annotation { "Feature Type Name" : "Feature", "Feature Type Description" : "" }
export const myFeature = defineFeature(function(context is Context, id is Id, definition is map)
    precondition{}
    {
        {
            var Q0;
            Q0=qCreatedBy(makeId("Top.planeOp"),FACE);
            var sketch = newSketch(context, id + "F0", { "sketchPlane" : qUnion([Q0])});
            skLineSegment(sketch, "E0.bottom", {"start": v(0, 0) * mm, "end": v(355.6, 0) * mm});
            skLineSegment(sketch, "E0.top", {"start": v(0, 50.8) * mm, "end": v(355.6, 50.8) * mm});
            skLineSegment(sketch, "E0.left", {"start": v(0, 0) * mm, "end": v(0, 50.8) * mm});
            skLineSegment(sketch, "E0.right", {"start": v(355.6, 0) * mm, "end": v(355.6, 50.8) * mm});
            skSolve(sketch);
        }
        {
            var Q0;
            Q0=makeQuery(id+"F0.imprint","IMPRINT",FACE,{"disambiguationData":[TD([[makeQuery(id+"F0.imprint","IMPRINT",EDGE,{"derivedFrom":sQuery(id+"F0.wireOp",EDGE,"E0.bottom")}),1.0]])]});
            extrude(context, id + "F1", {"entities" : qUnion([Q0]), "depth" : 6.35 * mm, "offsetDistance" : 25.4 * mm});
        }
        {
            var Q0;
            Q0=makeQuery(id+"F1.opExtrude","CAP_FACE",FACE,{"disambiguationData":[OSD([sQuery(id+"F0.wireOp",EDGE,"E0.bottom"),sQuery(id+"F0.wireOp",EDGE,"E0.top"),sQuery(id+"F0.wireOp",EDGE,"E0.left"),sQuery(id+"F0.wireOp",EDGE,"E0.right")])],"isStart":false});
            var sketch = newSketch(context, id + "F2", { "sketchPlane" : qUnion([Q0])});
            skText(sketch, "E1", { "text": "John Doe", "fontName": "OpenSans-BoldItalic.ttf"});
            const initialGuessF2  = {"E1": [0.06703, 0.01143, 1, 0, 0.02794]};
            skSetInitialGuess(sketch, initialGuessF2);
            skSolve(sketch);
        }
        {
            var Q0;
            Q0 = qSketchRegion(id + "F2", true);
            extrude(context, id + "F3", {"entities" : qUnion([Q0]), "operationType" : NewBodyOperationType.REMOVE, "oppositeDirection" : true, "depth" : 2.54 * mm, "offsetDistance" : 25.4 * mm});
        }
        {
            var Q0;
            {var subQ0=sQuery(id+"F0.wireOp",EDGE,"E0.top");var subQ1=sQuery(id+"F0.wireOp",EDGE,"E0.right");var subQ2=sQuery(id+"F0.wireOp",EDGE,"E0.bottom");var subQ3=sQuery(id+"F0.wireOp",EDGE,"E0.left");Q0=makeQuery(id+"F3.boolean.opBoolean","SPLIT",FACE,{"disambiguationData":[TD([makeQuery(id+"F1.opExtrude","SWEPT_FACE",FACE,{"disambiguationData":[OSD([subQ2])]})])],"derivedFrom":makeQuery(id+"F1.opExtrude","CAP_FACE",FACE,{"disambiguationData":[OSD([subQ2,subQ0,subQ3,subQ1])],"isStart":false})});}
            var sketch = newSketch(context, id + "F4", { "sketchPlane" : qUnion([Q0])});
            skCircle(sketch, "E2", {"center": v(311.15, 13.97) * mm, "radius": 5.08 * mm});
            skLineSegment(sketch, "E3", {"start": v(311.15, 13.97) * mm, "end": v(333.6, 36.42) * mm});
            skCircle(sketch, "E4.cCircle", {"center": v(335.4, 38.22) * mm, "radius": 2.54 * mm, "construction": true});
            skLineSegment(sketch, "E4.0", {"start": v(336.71, 33.3) * mm, "end": v(330.49, 39.53) * mm});
            skLineSegment(sketch, "E4.1", {"start": v(330.49, 39.53) * mm, "end": v(338.99, 41.8) * mm});
            skLineSegment(sketch, "E4.2", {"start": v(338.99, 41.8) * mm, "end": v(336.71, 33.3) * mm});
            skPoint(sketch, "E4.0.midPoint", {"position": v(333.6, 36.42) * mm});
            skCircle(sketch, "E5", {"center": v(311.15, 13.97) * mm, "radius": 7.62 * mm});
            skCircle(sketch, "E6", {"center": v(321.95, 38.1) * mm, "radius": 3.18 * mm});
            skCircle(sketch, "E7.cCircle", {"center": v(337.82, 26.03) * mm, "radius": 2.54 * mm, "construction": true});
            skLineSegment(sketch, "E7.0", {"start": v(341.41, 26.03) * mm, "end": v(337.82, 22.44) * mm});
            skLineSegment(sketch, "E7.1", {"start": v(337.82, 22.44) * mm, "end": v(334.23, 26.03) * mm});
            skLineSegment(sketch, "E7.2", {"start": v(334.23, 26.03) * mm, "end": v(337.82, 29.63) * mm});
            skLineSegment(sketch, "E7.3", {"start": v(337.82, 29.63) * mm, "end": v(341.41, 26.03) * mm});
            skPoint(sketch, "E7.0.midPoint", {"position": v(339.62, 24.24) * mm});
            skLineSegment(sketch, "E8", {"start": v(321.95, 38.1) * mm, "end": v(321.5, 38.55) * mm});
            skLineSegment(sketch, "E9", {"start": v(321.5, 38.55) * mm, "end": v(317.5, 34.55) * mm});
            skLineSegment(sketch, "E10", {"start": v(316.76, 32.53) * mm, "end": v(317.6, 22.96) * mm});
            skLineSegment(sketch, "E11", {"start": v(316.87, 20.95) * mm, "end": v(310.52, 14.6) * mm});
            skLineSegment(sketch, "E12", {"start": v(310.52, 14.6) * mm, "end": v(311.15, 13.97) * mm});
            skLineSegment(sketch, "E13", {"start": v(321.95, 38.1) * mm, "end": v(322.4, 37.65) * mm});
            skLineSegment(sketch, "E14", {"start": v(322.4, 37.65) * mm, "end": v(318.4, 33.65) * mm});
            skLineSegment(sketch, "E15", {"start": v(318.03, 32.65) * mm, "end": v(318.9, 22.79) * mm});
            skLineSegment(sketch, "E16", {"start": v(318.9, 22.79) * mm, "end": v(333.06, 36.96) * mm});
            skPoint(sketch, "E17.visualSharp", {"position": v(316.66, 33.71) * mm});
            skArc(sketch, "E17.filletArc", {"start": v(317.5, 34.55) * mm, "mid": v(316.9, 33.62) * mm, "end": v(316.76, 32.53) * mm});
            skPoint(sketch, "E18.visualSharp", {"position": v(317.98, 33.24) * mm});
            skArc(sketch, "E18.filletArc", {"start": v(318.4, 33.65) * mm, "mid": v(318.1, 33.2) * mm, "end": v(318.03, 32.65) * mm});
            skLineSegment(sketch, "E19", {"start": v(311.15, 13.97) * mm, "end": v(311.78, 13.34) * mm});
            skLineSegment(sketch, "E20", {"start": v(311.78, 13.34) * mm, "end": v(319.92, 21.48) * mm});
            skLineSegment(sketch, "E21", {"start": v(321.94, 22.22) * mm, "end": v(332.68, 21.28) * mm});
            skLineSegment(sketch, "E22", {"start": v(337.82, 26.03) * mm, "end": v(337.37, 26.48) * mm});
            skLineSegment(sketch, "E23", {"start": v(337.37, 26.48) * mm, "end": v(333.8, 22.91) * mm});
            skLineSegment(sketch, "E24", {"start": v(332.79, 22.54) * mm, "end": v(321.77, 23.5) * mm});
            skLineSegment(sketch, "E25", {"start": v(321.77, 23.5) * mm, "end": v(334.14, 35.88) * mm});
            skLineSegment(sketch, "E26", {"start": v(334.7, 22.01) * mm, "end": v(338.27, 25.59) * mm});
            skLineSegment(sketch, "E27", {"start": v(338.27, 25.59) * mm, "end": v(337.82, 26.03) * mm});
            skPoint(sketch, "E28.visualSharp", {"position": v(333.86, 21.18) * mm});
            skArc(sketch, "E28.filletArc", {"start": v(332.68, 21.28) * mm, "mid": v(333.77, 21.42) * mm, "end": v(334.7, 22.01) * mm});
            skPoint(sketch, "E29.visualSharp", {"position": v(320.76, 22.32) * mm});
            skArc(sketch, "E29.filletArc", {"start": v(321.94, 22.22) * mm, "mid": v(320.85, 22.07) * mm, "end": v(319.92, 21.48) * mm});
            skPoint(sketch, "E30.visualSharp", {"position": v(317.7, 21.78) * mm});
            skArc(sketch, "E30.filletArc", {"start": v(316.87, 20.95) * mm, "mid": v(317.46, 21.87) * mm, "end": v(317.6, 22.96) * mm});
            skPoint(sketch, "E31.visualSharp", {"position": v(333.38, 22.5) * mm});
            skArc(sketch, "E31.filletArc", {"start": v(332.79, 22.54) * mm, "mid": v(333.33, 22.62) * mm, "end": v(333.8, 22.91) * mm});
            skSolve(sketch);
        }
        {
            var Q0;
            Q0 = qSketchRegion(id + "F4", true);
            extrude(context, id + "F5", {"entities" : qUnion([Q0]), "operationType" : NewBodyOperationType.REMOVE, "oppositeDirection" : true, "depth" : 2.54 * mm, "offsetDistance" : 25.4 * mm});
        }
    });